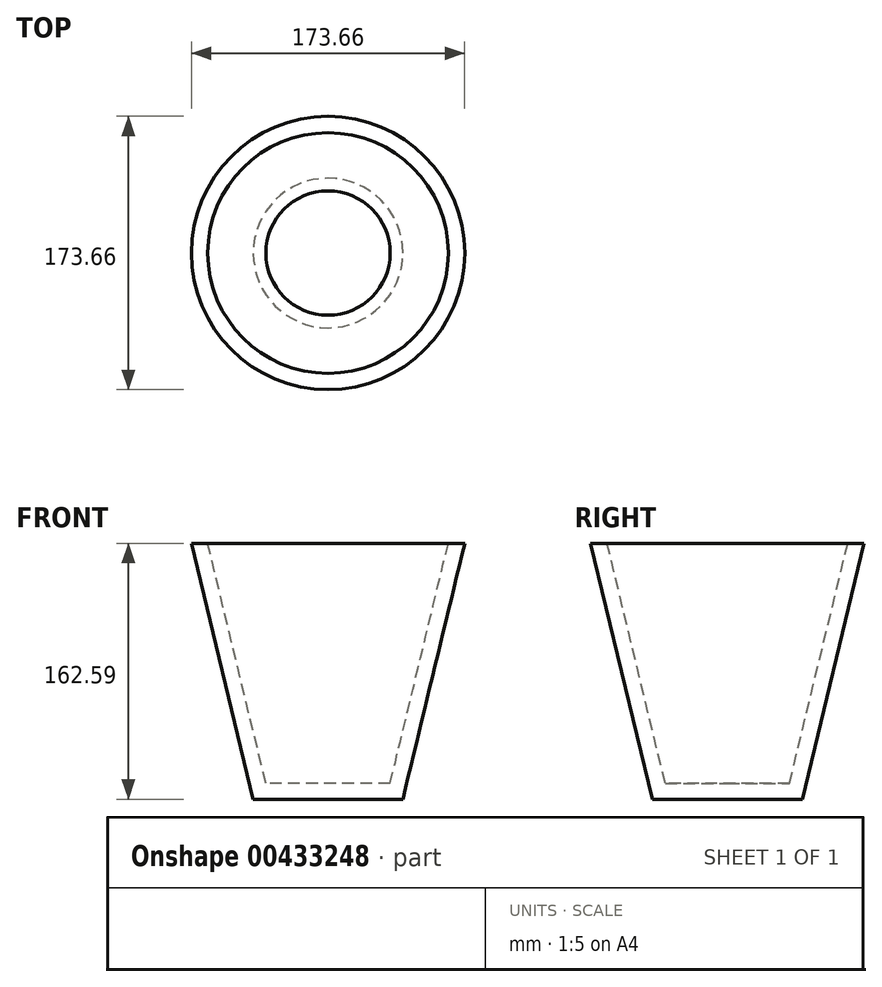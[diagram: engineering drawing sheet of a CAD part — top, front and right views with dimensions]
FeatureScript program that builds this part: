
annotation { "Feature Type Name" : "Feature", "Feature Type Description" : "" }
export const myFeature = defineFeature(function(context is Context, id is Id, definition is map)
    precondition{}
    {
        {
            var Q0;
            Q0=qCreatedBy(makeId("Front.planeOp"),FACE);
            var sketch = newSketch(context, id + "F0", { "sketchPlane" : qUnion([Q0])});
            skLineSegment(sketch, "E0", {"start": v(-76.38, 76.91) * mm, "end": v(0, 76.91) * mm});
            skLineSegment(sketch, "E1", {"start": v(0, 76.91) * mm, "end": v(0, -75.52) * mm});
            skLineSegment(sketch, "E2", {"start": v(0, -75.52) * mm, "end": v(-39.5, -75.52) * mm});
            skLineSegment(sketch, "E3", {"start": v(-39.5, -75.52) * mm, "end": v(-76.38, 76.91) * mm});
            skSolve(sketch);
        }
        {
            var Q0;
            Q0=makeQuery(id+"F0.imprint","IMPRINT",FACE,{"disambiguationData":[TD([[makeQuery(id+"F0.imprint","IMPRINT",EDGE,{"derivedFrom":sQuery(id+"F0.wireOp",EDGE,"E0")}),-1.0]])]});
            var Q1;
            Q1=sQuery(id+"F0.wireOp",EDGE,"E1");
            revolve(context, id + "F1", {"entities" : qUnion([Q0]), "axis" : qUnion([Q1]), "revolveType" : RevolveType.FULL});
        }
        {
            var Q0;
            Q0=makeQuery(id+"F1.opRevolve","SWEPT_FACE",FACE,{"disambiguationData":[OSD([sQuery(id+"F0.wireOp",EDGE,"E0")])]});
            shell(context, id + "F2", {"entities" : qUnion([Q0]), "thickness" : 10.16 * mm, "oppositeDirection" : true});
        }
    });
